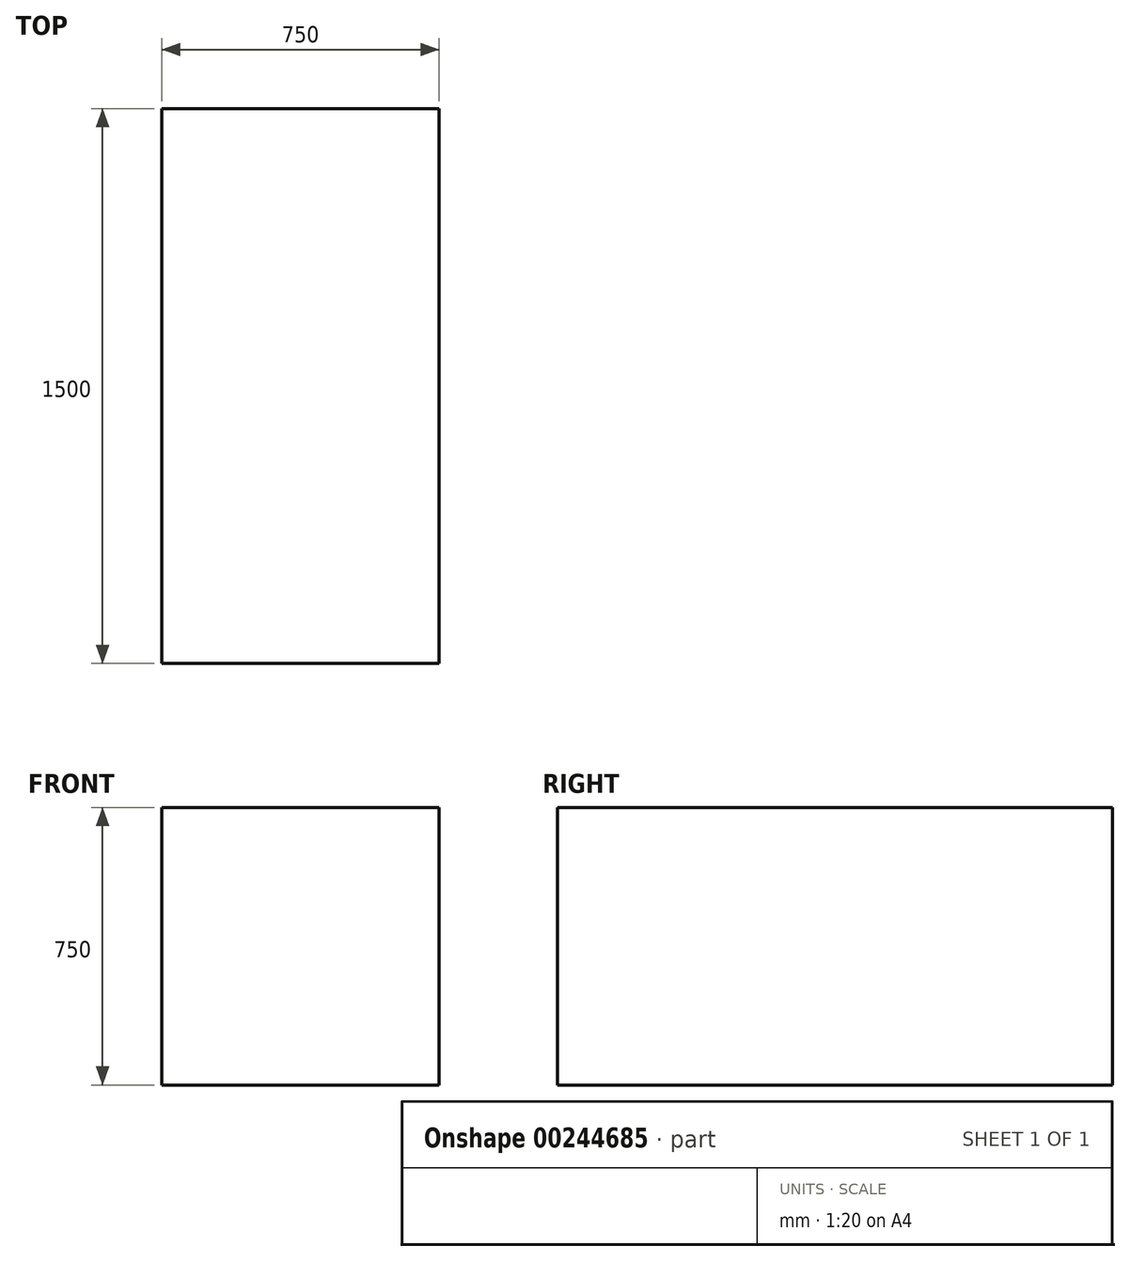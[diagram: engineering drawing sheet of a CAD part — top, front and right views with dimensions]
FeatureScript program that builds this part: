
annotation { "Feature Type Name" : "Feature", "Feature Type Description" : "" }
export const myFeature = defineFeature(function(context is Context, id is Id, definition is map)
    precondition{}
    {
        {
            var Q0;
            Q0=qCreatedBy(makeId("Top.planeOp"),FACE);
            var sketch = newSketch(context, id + "F0", { "sketchPlane" : qUnion([Q0])});
            skLineSegment(sketch, "E0.bottom", {"start": v(-375, 750) * mm, "end": v(375, 750) * mm});
            skLineSegment(sketch, "E0.top", {"start": v(-375, -750) * mm, "end": v(375, -750) * mm});
            skLineSegment(sketch, "E0.left", {"start": v(-375, 750) * mm, "end": v(-375, -750) * mm});
            skLineSegment(sketch, "E0.right", {"start": v(375, 750) * mm, "end": v(375, -750) * mm});
            skLineSegment(sketch, "E1", {"start": v(0, 1500) * mm, "end": v(0, 0) * mm, "construction": true});
            skLineSegment(sketch, "E2", {"start": v(0, 0) * mm, "end": v(750, 0) * mm, "construction": true});
            skPoint(sketch, "E3", {"position": v(-375, 0) * mm});
            skPoint(sketch, "E4", {"position": v(375, 0) * mm});
            skPoint(sketch, "E5", {"position": v(0, 750) * mm});
            skSolve(sketch);
        }
        {
            var Q0;
            Q0=makeQuery(id+"F0.imprint","IMPRINT",FACE,{"disambiguationData":[TD([[makeQuery(id+"F0.imprint","IMPRINT",EDGE,{"derivedFrom":sQuery(id+"F0.wireOp",EDGE,"E0.bottom")}),-1.0]])]});
            extrude(context, id + "F1", {"entities" : qUnion([Q0]), "depth" : 750 * mm});
        }
    });
